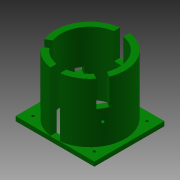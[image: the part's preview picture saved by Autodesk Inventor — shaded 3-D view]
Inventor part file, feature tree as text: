
AUTODESK INVENTOR PART (.ipt)
format: ipt  version: 2013 (Build 170138000, 138)  size: 341,504 bytes
history: native  units: mm
features: sketch x16, extrude x13, other x5, hole x3, pattern_circular x1
ambient origin geometry x8: Origin, YZ Plane, XZ Plane, XY Plane, X Axis, Y Axis, Z Axis, Center Point
feature tree (38):
  other  "ソリッド1"
  extrude  "押し出し1"  Depth=26.0mm
  extrude  "押し出し2"  Depth=20.0mm
  hole  "穴1"  [1 undecoded]
  pattern_circular  "円形状パターン1"  [2 undecoded]
  other  "作業平面21"
  extrude  "押し出し3"  Depth=10.8mm
  other  "作業平面18"
  hole  "穴2"  [1 undecoded]
  other  "作業平面17"
  extrude  "押し出し4"  Depth=145.0mm TaperAngle=0.0deg
  extrude  "押し出し5"  Depth=30.0mm TaperAngle=360.0deg
  extrude  "押し出し6"  Depth=19.5mm
  extrude  "押し出し7"  Depth=4.7mm
  other  "作業平面16"
  extrude  "押し出し8"  Depth=50.6mm
  extrude  "押し出し9"  Depth=3.0mm
  extrude  "押し出し10"  Depth=3.0mm
  extrude  "押し出し11"  Depth=5.1mm
  extrude  "押し出し12"  Depth=4.7mm
  hole  "穴3"  [1 undecoded]
  extrude  "押し出し13"  Depth=50.6mm
  sketch  "スケッチ1"
  sketch  "スケッチ2"
  sketch  "スケッチ3"
  sketch  "スケッチ5"
  sketch  "スケッチ6"
  sketch  "スケッチ7"
  sketch  "スケッチ8"
  sketch  "スケッチ9"
  sketch  "スケッチ10"
  sketch  "スケッチ12"
  sketch  "スケッチ13"
  sketch  "スケッチ14"
  sketch  "スケッチ15"
  sketch  "スケッチ16"
  sketch  "スケッチ17"
  sketch  "スケッチ18"
note: 5 required parameter values undecoded (feature->parameter linkage not recoverable at this tier; creation-order binding heuristic only, values carry confidence <= 0.55)
